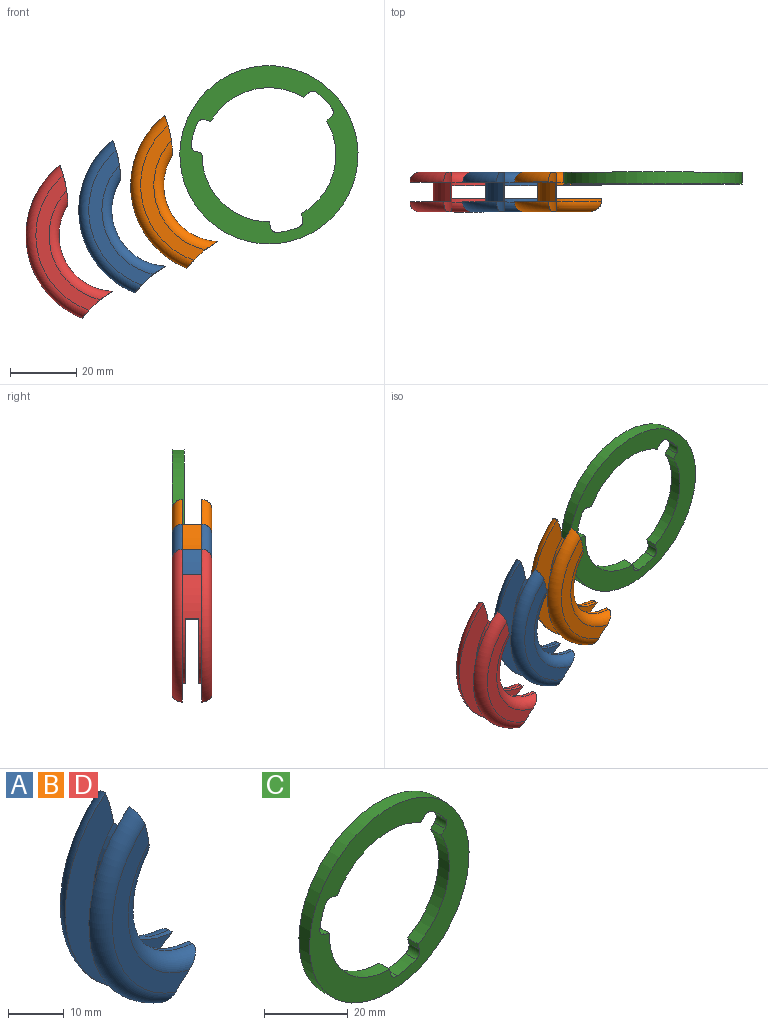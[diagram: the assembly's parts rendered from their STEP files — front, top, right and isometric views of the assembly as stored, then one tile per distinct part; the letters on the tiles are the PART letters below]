
ASSEMBLY  parts=4 mates=3
PART A: 16 faces, bbox 28.5x12x50.5 mm
  f0: cylinder r=20mm len=33.09mm, axis (0,1,0), area 142.1mm2, adj f1,f3,f4,f5,f7,f8,f9,f11
  f1: cylinder r=10mm len=4mm, axis (0,1,0), area 12.1mm2, adj f0,f2,f7,f11
  f2: cylinder r=17mm len=26.09mm, axis (0,1,0), area 109.6mm2, adj f1,f3,f5,f7,f9,f11,f12,f15
  f3: cylinder r=32mm len=12.09mm, axis (0,1,0), area 90.9mm2, adj f0,f2,f4,f6,f8,f10,f12,f13
  f4: plane 46.28x22.57mm, normal (0,-1,0), area 344.5mm2, adj f0,f3,f5,f14
  f5: cylinder r=32mm len=9.29mm, axis (0,-1,0), area 36.5mm2, adj f0,f2,f4,f6,f7,f14,f15
  f6: plane 40.84x19.57mm, normal (0,1,0), area 184.3mm2, adj f3,f5,f14,f15
  f7: plane 19.87x19.3mm, normal (0,-1,0), area 79.3mm2, adj f0,f1,f2,f5
  f8: plane 46.28x22.57mm, normal (0,1,0), area 344.5mm2, adj f0,f3,f9,f13
  f9: cylinder r=32mm len=9.29mm, axis (0,1,0), area 36.5mm2, adj f0,f2,f8,f10,f11,f12,f13
  f10: plane 40.84x19.57mm, normal (0,-1,0), area 184.3mm2, adj f3,f9,f12,f13
  f11: plane 19.87x19.3mm, normal (0,1,0), area 79.3mm2, adj f0,f1,f2,f9
  f12: torus R=20mm, axis (0,1,0), area 178.5mm2, adj f2,f3,f9,f10
  f13: torus R=24mm, axis (0,1,0), area 255.7mm2, adj f3,f8,f9,f10
  f14: torus R=24mm, axis (0,-1,0), area 255.7mm2, adj f3,f4,f5,f6
  f15: torus R=20mm, axis (0,-1,0), area 178.5mm2, adj f2,f3,f5,f6
PART B: same geometry as A
PART C: 21 faces, bbox 54x3.6x54 mm
  f0: plane 54x54mm, normal (0,-1,0), area 894.9mm2, adj f2,f3,f4,f5,f6,f7,f8,f9
  f1: plane 54x54mm, normal (0,1,0), area 894.9mm2, adj f2,f3,f4,f5,f6,f7,f8,f9
  f2: cylinder r=20.3mm len=28.15mm, axis (0,1,0), area 116.7mm2, adj f0,f1,f9,f13
  f3: cylinder r=20.3mm len=28.02mm, axis (0,1,0), area 116.7mm2, adj f0,f1,f12,f14
  f4: cylinder r=27mm len=54mm, axis (0,1,0), area 610.7mm2, adj f0,f1
  f5: cylinder r=20.3mm len=20.75mm, axis (0,1,0), area 116.7mm2, adj f0,f1,f6,f10
  f6: plane 3.6x1.8mm, normal (0.97,0,0.25), area 6.7mm2, adj f0,f1,f5,f16
  f7: cylinder r=23.74mm len=6.34mm, axis (0,-1,0), area 23.7mm2, adj f0,f1,f15,f16
  f8: cylinder r=23.74mm len=4.68mm, axis (0,-1,0), area 23.7mm2, adj f0,f1,f17,f18
  f9: plane 3.6x1.33mm, normal (0.7,0,-0.71), area 6.7mm2, adj f0,f1,f2,f17
  f10: plane 3.6x1.79mm, normal (0.27,0,0.96), area 6.7mm2, adj f0,f1,f5,f20
  f11: cylinder r=23.74mm len=6.31mm, axis (0,-1,0), area 23.7mm2, adj f0,f1,f19,f20
  f12: plane 3.6x1.33mm, normal (-0.7,0,0.71), area 6.7mm2, adj f0,f1,f3,f18
  f13: plane 3.6x1.79mm, normal (-0.27,0,-0.96), area 6.7mm2, adj f0,f1,f2,f19
  f14: plane 3.6x1.8mm, normal (-0.97,0,-0.25), area 6.7mm2, adj f0,f1,f3,f15
  f15: cylinder r=2mm len=3.6mm, axis (0,-1,0), area 10.3mm2, adj f0,f1,f7,f14
  f16: cylinder r=2mm len=3.6mm, axis (0,-1,0), area 10.3mm2, adj f0,f1,f6,f7
  f17: cylinder r=2mm len=3.6mm, axis (0,-1,0), area 10.3mm2, adj f0,f1,f8,f9
  f18: cylinder r=2mm len=3.6mm, axis (0,-1,0), area 10.3mm2, adj f0,f1,f8,f12
  f19: cylinder r=2mm len=3.6mm, axis (0,-1,0), area 10.3mm2, adj f0,f1,f11,f13
  f20: cylinder r=2mm len=3.6mm, axis (0,-1,0), area 10.3mm2, adj f0,f1,f10,f11
PART D: same geometry as A
PLACE A t=(-40.36,-9,-20.03)mm
PLACE B t=(-24.64,-9,-12.57)mm
PLACE C t=(-9.76,-5.8,-3.26)mm fixed
PLACE D t=(-56.37,-9,-27.67)mm
MATE planar C.f1 <-> B.f6  axis (0,1,0) through (-30.95,-6,-2.56)mm
MATE planar B.f10 <-> A.f10  axis (0,-1,0) through (-39.32,-18,1.02)mm
MATE planar D.f10 <-> B.f10  axis (0,-1,0) through (-71.05,-18,-14.09)mm
